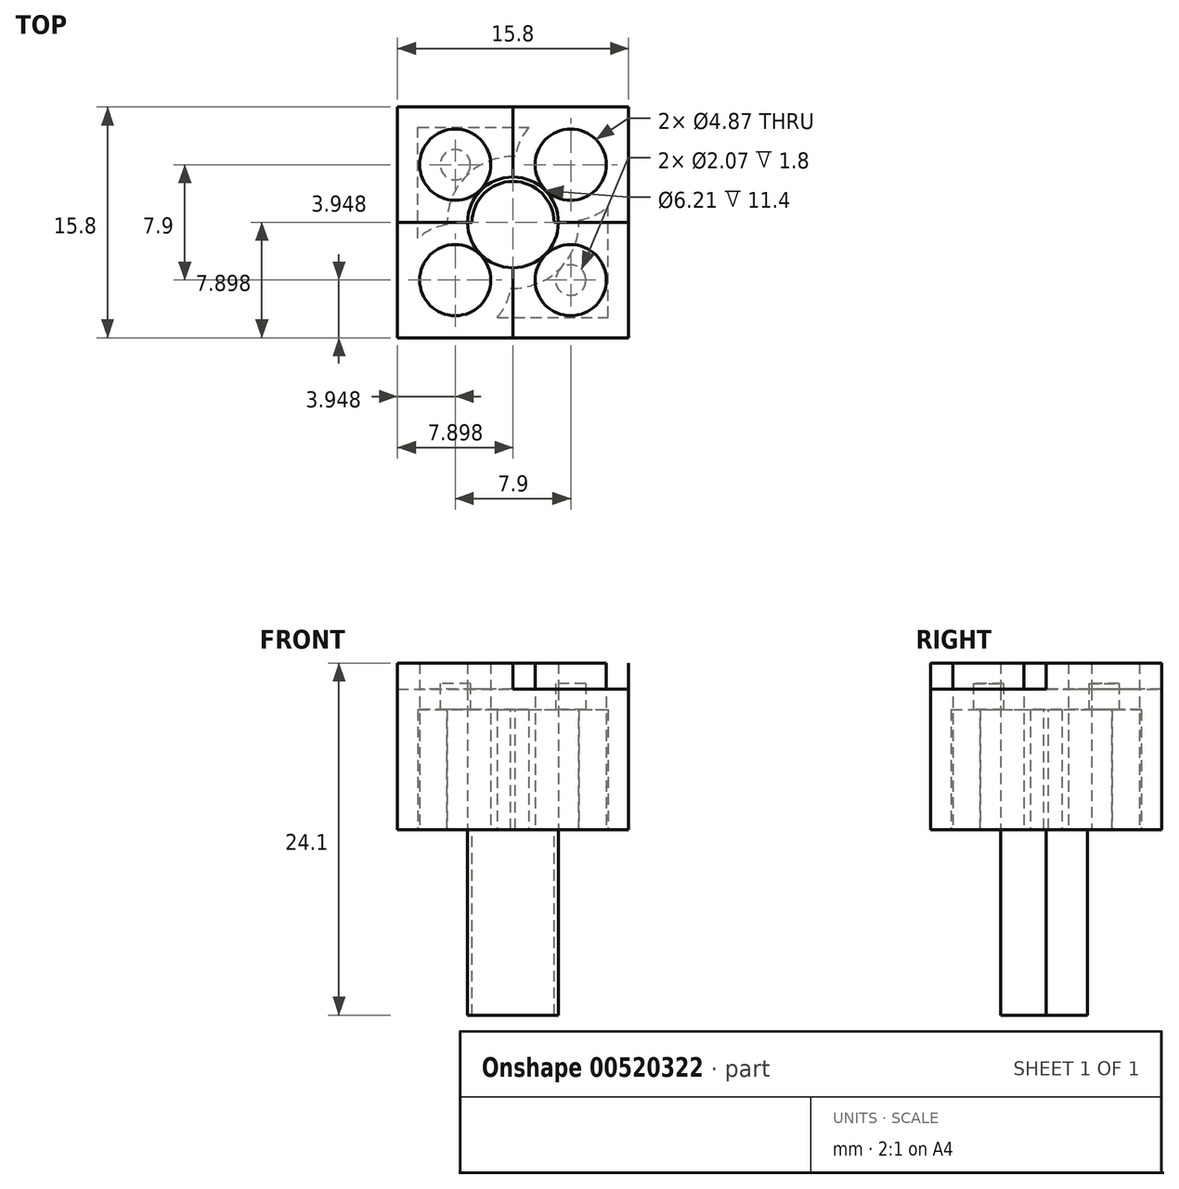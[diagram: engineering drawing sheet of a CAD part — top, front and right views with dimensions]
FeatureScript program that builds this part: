
annotation { "Feature Type Name" : "Feature", "Feature Type Description" : "" }
export const myFeature = defineFeature(function(context is Context, id is Id, definition is map)
    precondition{}
    {
        {
            var Q0;
            Q0=qCreatedBy(makeId("Top.planeOp"),FACE);
            var sketch = newSketch(context, id + "F0", { "sketchPlane" : qUnion([Q0])});
            skLineSegment(sketch, "E0.bottom", {"start": v(-47.07, 36.12) * mm, "end": v(-31.27, 36.12) * mm});
            skLineSegment(sketch, "E0.top", {"start": v(-47.07, 51.92) * mm, "end": v(-31.27, 51.92) * mm});
            skLineSegment(sketch, "E0.left", {"start": v(-47.07, 36.12) * mm, "end": v(-47.07, 51.92) * mm});
            skLineSegment(sketch, "E0.right", {"start": v(-31.27, 36.12) * mm, "end": v(-31.27, 51.92) * mm});
            skLineSegment(sketch, "E1", {"start": v(-45.57, 47.97) * mm, "end": v(-45.56, 47.97) * mm});
            skCircle(sketch, "E2", {"center": v(-43.12, 47.97) * mm, "radius": 2.44 * mm});
            skLineSegment(sketch, "E3", {"start": v(-39.17, 36.12) * mm, "end": v(-39.17, 51.92) * mm});
            skLineSegment(sketch, "E4", {"start": v(-39.17, 51.92) * mm, "end": v(-39.17, 44.02) * mm});
            skLineSegment(sketch, "E5", {"start": v(-39.17, 44.02) * mm, "end": v(-31.27, 44.02) * mm});
            skLineSegment(sketch, "E6", {"start": v(-31.27, 44.02) * mm, "end": v(-47.07, 44.02) * mm});
            skCircle(sketch, "E7.MirrorC", {"center": v(-35.22, 47.97) * mm, "radius": 2.44 * mm});
            skLineSegment(sketch, "E8.MirrorCS", {"start": v(-47.07, 44.02) * mm, "end": v(-31.27, 44.02) * mm});
            skCircle(sketch, "E9.MirrorC", {"center": v(-43.12, 40.07) * mm, "radius": 2.44 * mm});
            skCircle(sketch, "E10.MirrorC", {"center": v(-35.22, 40.07) * mm, "radius": 2.44 * mm});
            skCircle(sketch, "E11", {"center": v(-39.17, 44.02) * mm, "radius": 3.1 * mm});
            skCircle(sketch, "E12.0", {"center": v(-39.17, 44.02) * mm, "radius": 2.8 * mm});
            skSolve(sketch);
        }
        {
            var Q0;
            Q0 = qSketchRegion(id + "F0", true);
            extrude(context, id + "F1", {"entities" : qUnion([Q0]), "depth" : 9.6 * mm, "offsetDistance" : 25 * mm});
        }
        {
            var Q0;
            Q0=makeQuery(id+"F0.imprint","IMPRINT",FACE,{"disambiguationData":[TD([[makeQuery(id+"F0.imprint","IMPRINT",EDGE,{"derivedFrom":sQuery(id+"F0.wireOp",EDGE,"E10.MirrorC")}),1.0]])]});
            var Q1;
            Q1=makeQuery(id+"F0.imprint","IMPRINT",FACE,{"disambiguationData":[TD([[makeQuery(id+"F0.imprint","IMPRINT",EDGE,{"derivedFrom":sQuery(id+"F0.wireOp",EDGE,"E7.MirrorC")}),-1.0]])]});
            var Q2;
            Q2=makeQuery(id+"F0.imprint","IMPRINT",FACE,{"disambiguationData":[TD([[makeQuery(id+"F0.imprint","IMPRINT",EDGE,{"derivedFrom":sQuery(id+"F0.wireOp",EDGE,"E2")}),1.0]])]});
            var Q3;
            Q3=makeQuery(id+"F0.imprint","IMPRINT",FACE,{"disambiguationData":[TD([[makeQuery(id+"F0.imprint","IMPRINT",EDGE,{"derivedFrom":sQuery(id+"F0.wireOp",EDGE,"E9.MirrorC")}),-1.0]])]});
            extrude(context, id + "F2", {"entities" : qUnion([Q0, Q1, Q2, Q3]), "operationType" : NewBodyOperationType.ADD, "depth" : 11.4 * mm, "offsetDistance" : 25 * mm});
        }
        {
            var Q0;
            {var subQ0=sQuery(id+"F0.wireOp",EDGE,"E10.MirrorC");var subQ1=sQuery(id+"F0.wireOp",EDGE,"E9.MirrorC");var subQ2=sQuery(id+"F0.wireOp",EDGE,"E7.MirrorC");var subQ3=sQuery(id+"F0.wireOp",EDGE,"E2");Q0=makeQuery(id+"F2.boolean.opBoolean","MERGE",FACE,{"derivedFrom":[makeQuery(id+"F1.opExtrude","CAP_FACE",FACE,{"disambiguationData":[OSD([sQuery(id+"F0.wireOp",EDGE,"E0.bottom"),sQuery(id+"F0.wireOp",EDGE,"E0.top"),sQuery(id+"F0.wireOp",EDGE,"E0.left"),sQuery(id+"F0.wireOp",EDGE,"E0.right"),subQ3,subQ2,subQ1,subQ0])],"isStart":true}),makeQuery(id+"F2.opExtrude","CAP_FACE",FACE,{"disambiguationData":[OSD([subQ3])],"isStart":true}),makeQuery(id+"F2.opExtrude","CAP_FACE",FACE,{"disambiguationData":[OSD([subQ2])],"isStart":true}),makeQuery(id+"F2.opExtrude","CAP_FACE",FACE,{"disambiguationData":[OSD([subQ1])],"isStart":true}),makeQuery(id+"F2.opExtrude","CAP_FACE",FACE,{"disambiguationData":[OSD([subQ0])],"isStart":true})]});}
            shell(context, id + "F3", {"entities" : qUnion([Q0]), "thickness" : 1.4 * mm});
        }
        {
            var Q0;
            {var subQ1=sQuery(id+"F0.wireOp",EDGE,"E3");var subQ3=sQuery(id+"F0.wireOp",EDGE,"E12.0");var subQ4=makeQuery(id+"F0.imprint","INTERSECT",VERTEX,{"derivedFrom":[subQ1,subQ3]});Q0=makeQuery(id+"F0.imprint","IMPRINT",FACE,{"disambiguationData":[TD([[makeQuery(id+"F0.imprint","IMPRINT",EDGE,{"disambiguationData":[TD([[subQ4,1.0]])],"derivedFrom":subQ3}),1.0]])]});}
            var Q1;
            {var subQ1=sQuery(id+"F0.wireOp",EDGE,"E4");var subQ3=sQuery(id+"F0.wireOp",EDGE,"E12.0");var subQ4=makeQuery(id+"F0.imprint","INTERSECT",VERTEX,{"derivedFrom":[subQ1,subQ3]});Q1=makeQuery(id+"F0.imprint","IMPRINT",FACE,{"disambiguationData":[TD([[makeQuery(id+"F0.imprint","IMPRINT",EDGE,{"disambiguationData":[TD([[subQ4,-1.0]])],"derivedFrom":subQ3}),1.0]])]});}
            var Q2;
            {var subQ1=sQuery(id+"F0.wireOp",EDGE,"E4");var subQ3=sQuery(id+"F0.wireOp",EDGE,"E12.0");var subQ4=makeQuery(id+"F0.imprint","INTERSECT",VERTEX,{"derivedFrom":[subQ1,subQ3]});Q2=makeQuery(id+"F0.imprint","IMPRINT",FACE,{"disambiguationData":[TD([[makeQuery(id+"F0.imprint","IMPRINT",EDGE,{"disambiguationData":[TD([[subQ4,1.0]])],"derivedFrom":subQ3}),1.0]])]});}
            var Q3;
            {var subQ1=sQuery(id+"F0.wireOp",EDGE,"E3");var subQ3=sQuery(id+"F0.wireOp",EDGE,"E12.0");var subQ4=makeQuery(id+"F0.imprint","INTERSECT",VERTEX,{"derivedFrom":[subQ1,subQ3]});Q3=makeQuery(id+"F0.imprint","IMPRINT",FACE,{"disambiguationData":[TD([[makeQuery(id+"F0.imprint","IMPRINT",EDGE,{"disambiguationData":[TD([[subQ4,-1.0]])],"derivedFrom":subQ3}),1.0]])]});}
            var Q4;
            {var subQ0=sQuery(id+"F0.wireOp",EDGE,"E11");var subQ1=sQuery(id+"F0.wireOp",EDGE,"E4");var subQ2=makeQuery(id+"F0.imprint","INTERSECT",VERTEX,{"derivedFrom":[subQ1,subQ0]});Q4=makeQuery(id+"F0.imprint","IMPRINT",FACE,{"disambiguationData":[TD([[makeQuery(id+"F0.imprint","IMPRINT",EDGE,{"disambiguationData":[TD([[subQ2,-1.0]])],"derivedFrom":subQ1}),1.0]])]});}
            var Q5;
            {var subQ0=sQuery(id+"F0.wireOp",EDGE,"E11");var subQ1=sQuery(id+"F0.wireOp",EDGE,"E4");var subQ2=makeQuery(id+"F0.imprint","INTERSECT",VERTEX,{"derivedFrom":[subQ1,subQ0]});Q5=makeQuery(id+"F0.imprint","IMPRINT",FACE,{"disambiguationData":[TD([[makeQuery(id+"F0.imprint","IMPRINT",EDGE,{"disambiguationData":[TD([[subQ2,-1.0]])],"derivedFrom":subQ1}),-1.0]])]});}
            var Q6;
            {var subQ0=sQuery(id+"F0.wireOp",EDGE,"E11");var subQ1=sQuery(id+"F0.wireOp",EDGE,"E3");var subQ2=makeQuery(id+"F0.imprint","INTERSECT",VERTEX,{"derivedFrom":[subQ1,subQ0]});Q6=makeQuery(id+"F0.imprint","IMPRINT",FACE,{"disambiguationData":[TD([[makeQuery(id+"F0.imprint","IMPRINT",EDGE,{"disambiguationData":[TD([[subQ2,-1.0]])],"derivedFrom":subQ1}),-1.0]])]});}
            var Q7;
            {var subQ0=sQuery(id+"F0.wireOp",EDGE,"E11");var subQ1=sQuery(id+"F0.wireOp",EDGE,"E3");var subQ2=makeQuery(id+"F0.imprint","INTERSECT",VERTEX,{"derivedFrom":[subQ1,subQ0]});Q7=makeQuery(id+"F0.imprint","IMPRINT",FACE,{"disambiguationData":[TD([[makeQuery(id+"F0.imprint","IMPRINT",EDGE,{"disambiguationData":[TD([[subQ2,-1.0]])],"derivedFrom":subQ1}),1.0]])]});}
            extrude(context, id + "F4", {"entities" : qUnion([Q0, Q1, Q2, Q3, Q4, Q5, Q6, Q7]), "oppositeDirection" : true, "depth" : 12.7 * mm, "offsetDistance" : 25 * mm});
        }
    });
